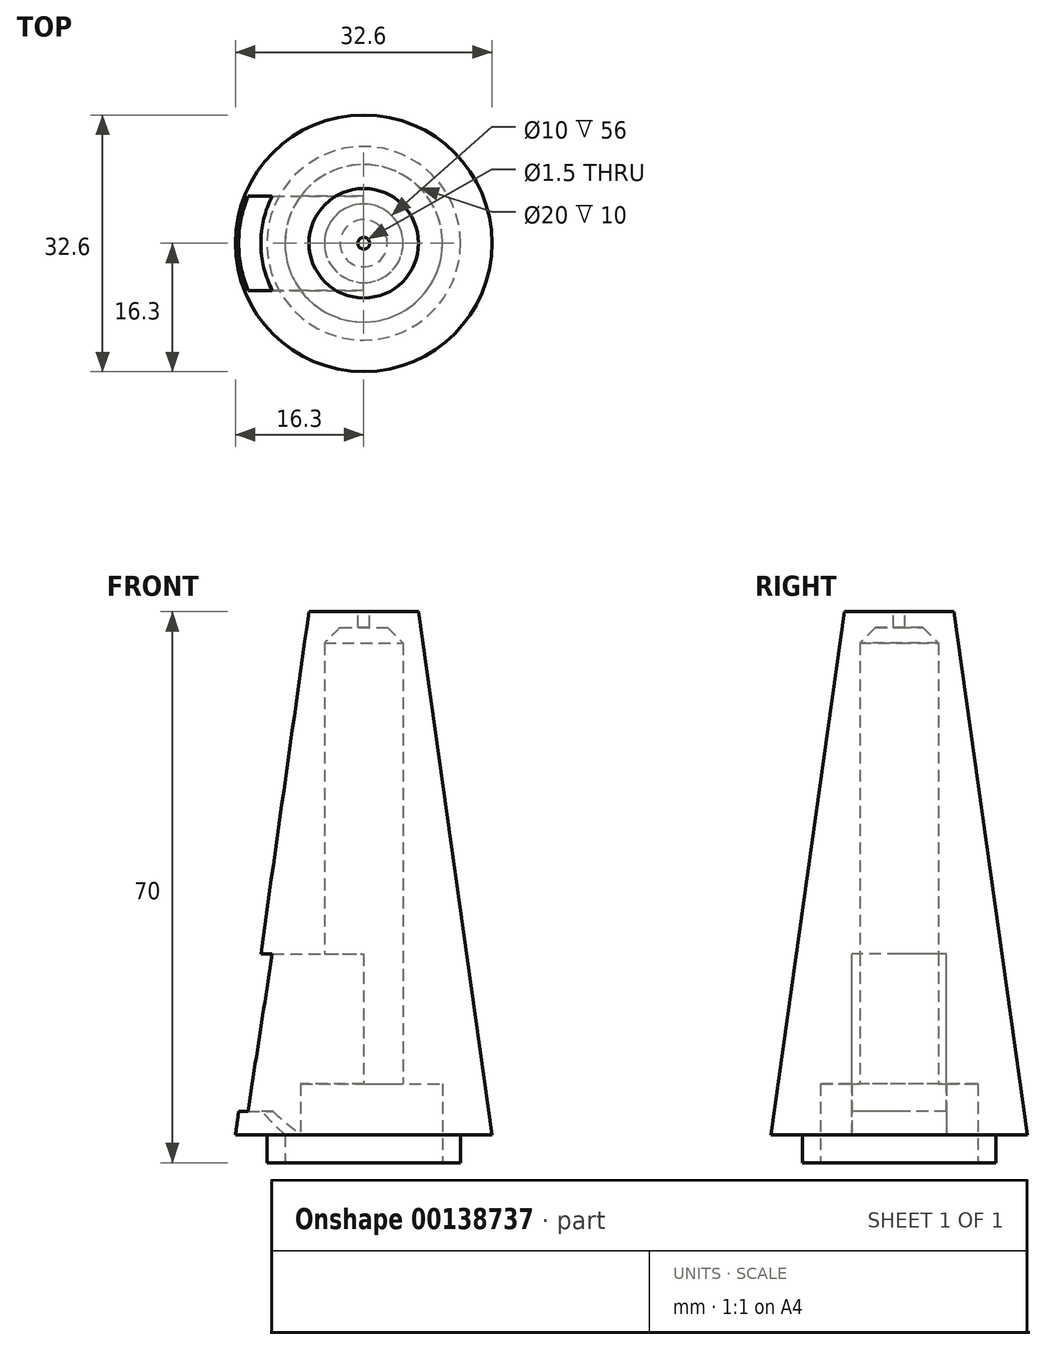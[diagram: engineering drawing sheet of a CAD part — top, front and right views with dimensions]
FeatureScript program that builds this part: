
annotation { "Feature Type Name" : "Feature", "Feature Type Description" : "" }
export const myFeature = defineFeature(function(context is Context, id is Id, definition is map)
    precondition{}
    {
        {
            var Q0;
            Q0=qCreatedBy(makeId("Front.planeOp"),FACE);
            var sketch = newSketch(context, id + "F0", { "sketchPlane" : qUnion([Q0])});
            skLineSegment(sketch, "E0", {"start": v(0, 26.64) * mm, "end": v(6.95, 26.64) * mm});
            skLineSegment(sketch, "E1", {"start": v(6.95, 26.64) * mm, "end": v(16.3, -39.86) * mm});
            skLineSegment(sketch, "E2", {"start": v(16.3, -39.86) * mm, "end": v(12.3, -39.86) * mm});
            skLineSegment(sketch, "E3", {"start": v(12.3, -39.86) * mm, "end": v(12.3, -43.36) * mm});
            skLineSegment(sketch, "E4", {"start": v(12.3, -43.36) * mm, "end": v(5, -43.36) * mm});
            skLineSegment(sketch, "E5", {"start": v(5, -43.36) * mm, "end": v(5, 22.64) * mm});
            skLineSegment(sketch, "E6", {"start": v(5, 22.64) * mm, "end": v(3, 24.64) * mm});
            skLineSegment(sketch, "E7", {"start": v(3, 24.64) * mm, "end": v(0, 24.64) * mm});
            skLineSegment(sketch, "E8", {"start": v(0, 24.64) * mm, "end": v(0, 26.64) * mm});
            skSolve(sketch);
        }
        {
            var Q0;
            Q0 = qSketchRegion(id + "F0", true);
            var Q1;
            Q1=sQuery(id+"F0.wireOp",EDGE,"E8");
            revolve(context, id + "F1", {"entities" : qUnion([Q0]), "axis" : qUnion([Q1]), "revolveType" : RevolveType.FULL});
        }
        {
            var Q0;
            Q0=makeQuery(id+"F1.opRevolve","SWEPT_FACE",FACE,{"disambiguationData":[OSD([sQuery(id+"F0.wireOp",EDGE,"E0")])]});
            var sketch = newSketch(context, id + "F2", { "sketchPlane" : qUnion([Q0])});
            skCircle(sketch, "E9", {"center": v(0, 0) * mm, "radius": 0.75 * mm});
            skSolve(sketch);
        }
        {
            var Q0;
            Q0 = qSketchRegion(id + "F2", true);
            extrude(context, id + "F3", {"entities" : qUnion([Q0]), "operationType" : NewBodyOperationType.REMOVE, "endBound" : BoundingType.THROUGH_ALL, "oppositeDirection" : true, "depth" : 25 * mm});
        }
        {
            var Q0;
            Q0=qCreatedBy(makeId("Right.planeOp"),FACE);
            var sketch = newSketch(context, id + "F4", { "sketchPlane" : qUnion([Q0])});
            skLineSegment(sketch, "E10.bottom", {"start": v(6, -36.86) * mm, "end": v(-6, -36.86) * mm});
            skLineSegment(sketch, "E10.top", {"start": v(6, -16.86) * mm, "end": v(-6, -16.86) * mm});
            skLineSegment(sketch, "E10.left", {"start": v(6, -36.86) * mm, "end": v(6, -16.86) * mm});
            skLineSegment(sketch, "E10.right", {"start": v(-6, -36.86) * mm, "end": v(-6, -16.86) * mm});
            skSolve(sketch);
        }
        {
            var Q0;
            Q0 = qSketchRegion(id + "F4", true);
            extrude(context, id + "F5", {"entities" : qUnion([Q0]), "operationType" : NewBodyOperationType.REMOVE, "oppositeDirection" : true, "depth" : 25 * mm});
        }
        {
            var Q0;
            Q0=makeQuery(id+"F1.opRevolve","SWEPT_FACE",FACE,{"disambiguationData":[OSD([sQuery(id+"F0.wireOp",EDGE,"E4")])]});
            var sketch = newSketch(context, id + "F6", { "sketchPlane" : qUnion([Q0])});
            skCircle(sketch, "E11", {"center": v(0, 0) * mm, "radius": 10 * mm});
            skSolve(sketch);
        }
        {
            var Q0;
            Q0 = qSketchRegion(id + "F6", true);
            extrude(context, id + "F7", {"entities" : qUnion([Q0]), "operationType" : NewBodyOperationType.REMOVE, "oppositeDirection" : true, "depth" : 10 * mm});
        }
        {
            var Q0;
            Q0=makeQuery(id+"F7.boolean.opBoolean","INTERSECT",EDGE,{"derivedFrom":[makeQuery(id+"F5.boolean.opBoolean","COPY",FACE,{"derivedFrom":makeQuery(id+"F5.opExtrude","SWEPT_FACE",FACE,{"disambiguationData":[OSD([sQuery(id+"F4.wireOp",EDGE,"E10.bottom")])]})}),makeQuery(id+"F7.opExtrude","SWEPT_FACE",FACE,{"disambiguationData":[OSD([sQuery(id+"F6.wireOp",EDGE,"E11")])]})]});
            chamfer(context, id + "F8", {"entities" : qUnion([Q0]), "width" : 3 * mm, "tangentPropagation" : true});
        }
    });
